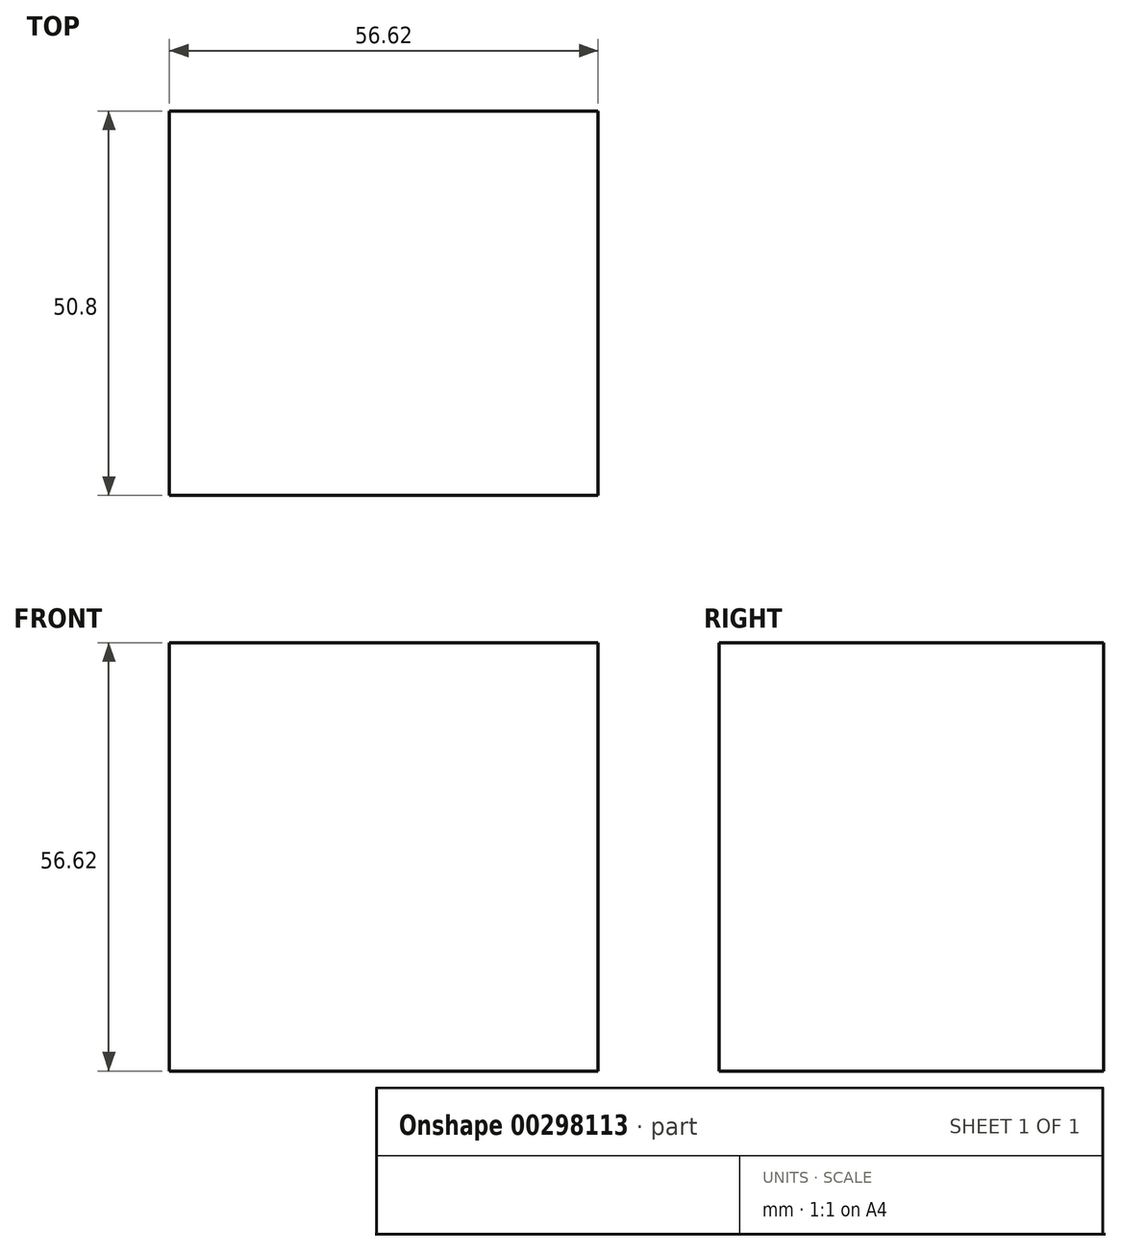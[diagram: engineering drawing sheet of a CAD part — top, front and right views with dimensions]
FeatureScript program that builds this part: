
annotation { "Feature Type Name" : "Feature", "Feature Type Description" : "" }
export const myFeature = defineFeature(function(context is Context, id is Id, definition is map)
    precondition{}
    {
        {
            var Q0;
            Q0=qCreatedBy(makeId("Front.planeOp"),FACE);
            var sketch = newSketch(context, id + "F0", { "sketchPlane" : qUnion([Q0])});
            skLineSegment(sketch, "E0.bottom", {"start": v(0, 0) * mm, "end": v(56.62, 0) * mm});
            skLineSegment(sketch, "E0.top", {"start": v(0, 56.62) * mm, "end": v(56.62, 56.62) * mm});
            skLineSegment(sketch, "E0.left", {"start": v(0, 0) * mm, "end": v(0, 56.62) * mm});
            skLineSegment(sketch, "E0.right", {"start": v(56.62, 0) * mm, "end": v(56.62, 56.62) * mm});
            skSolve(sketch);
        }
        {
            var Q0;
            Q0=makeQuery(id+"F0.imprint","IMPRINT",FACE,{"disambiguationData":[TD([[makeQuery(id+"F0.imprint","IMPRINT",EDGE,{"derivedFrom":sQuery(id+"F0.wireOp",EDGE,"E0.bottom")}),1.0]])]});
            extrude(context, id + "F1", {"entities" : qUnion([Q0]), "depth" : 50.8 * mm});
        }
    });
